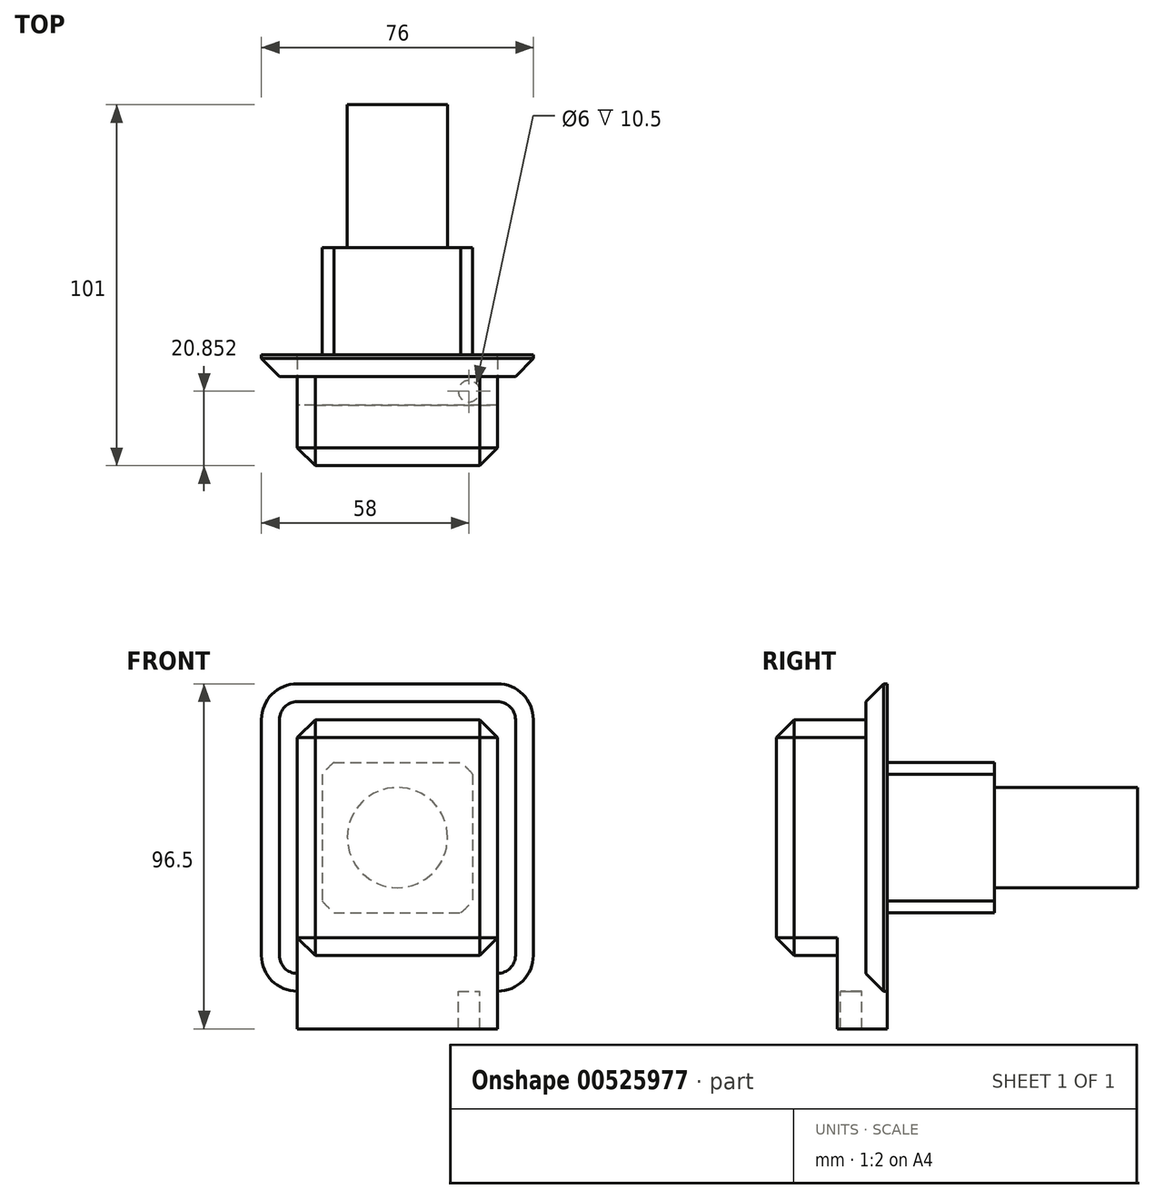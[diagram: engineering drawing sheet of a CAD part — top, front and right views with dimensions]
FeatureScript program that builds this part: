
annotation { "Feature Type Name" : "Feature", "Feature Type Description" : "" }
export const myFeature = defineFeature(function(context is Context, id is Id, definition is map)
    precondition{}
    {
        {
            var Q0;
            Q0=qCreatedBy(makeId("Front.planeOp"),FACE);
            var sketch = newSketch(context, id + "F0", { "sketchPlane" : qUnion([Q0])});
            skLineSegment(sketch, "E0.bottom", {"start": v(28, 43) * mm, "end": v(-28, 43) * mm});
            skLineSegment(sketch, "E0.top", {"start": v(28, -43) * mm, "end": v(-28, -43) * mm});
            skLineSegment(sketch, "E0.left", {"start": v(38, 33) * mm, "end": v(38, -33) * mm});
            skLineSegment(sketch, "E0.right", {"start": v(-38, 33) * mm, "end": v(-38, -33) * mm});
            skPoint(sketch, "E0.middle", {"position": v(0, 0) * mm});
            skPoint(sketch, "E1.visualSharp", {"position": v(-38, 43) * mm});
            skArc(sketch, "E1.filletArc", {"start": v(-28, 43) * mm, "mid": v(-35.07, 40.07) * mm, "end": v(-38, 33) * mm});
            skPoint(sketch, "E2.visualSharp", {"position": v(38, 43) * mm});
            skArc(sketch, "E2.filletArc", {"start": v(38, 33) * mm, "mid": v(35.07, 40.07) * mm, "end": v(28, 43) * mm});
            skPoint(sketch, "E3.visualSharp", {"position": v(38, -43) * mm});
            skArc(sketch, "E3.filletArc", {"start": v(28, -43) * mm, "mid": v(35.07, -40.07) * mm, "end": v(38, -33) * mm});
            skPoint(sketch, "E4.visualSharp", {"position": v(-38, -43) * mm});
            skArc(sketch, "E4.filletArc", {"start": v(-38, -33) * mm, "mid": v(-35.07, -40.07) * mm, "end": v(-28, -43) * mm});
            skSolve(sketch);
        }
        {
            var Q0;
            Q0=qSketchRegion(id+"F0",true);
            extrude(context, id + "F1", {"entities" : qUnion([Q0]), "depth" : 6 * mm, "offsetDistance" : 25 * mm});
        }
        {
            var Q0;
            Q0=makeQuery(id+"F1.opExtrude","CAP_FACE",FACE,{"disambiguationData":[OSD([sQuery(id+"F0.wireOp",EDGE,"E0.bottom"),sQuery(id+"F0.wireOp",EDGE,"E0.top"),sQuery(id+"F0.wireOp",EDGE,"E0.left"),sQuery(id+"F0.wireOp",EDGE,"E0.right")])],"isStart":true});
            var sketch = newSketch(context, id + "F2", { "sketchPlane" : qUnion([Q0])});
            skCircle(sketch, "E5", {"center": v(0, 0) * mm, "radius": 27.5 * mm});
            skSolve(sketch);
        }
        {
            var Q0;
            Q0=qSketchRegion(id+"F2",true);
            extrude(context, id + "F3", {"entities" : qUnion([Q0]), "operationType" : NewBodyOperationType.ADD, "depth" : 30 * mm});
        }
        {
            var Q0;
            Q0=makeQuery(id+"F3.opExtrude","CAP_FACE",FACE,{"disambiguationData":[OSD([sQuery(id+"F2.wireOp",EDGE,"E5")])],"isStart":false});
            var sketch = newSketch(context, id + "F4", { "sketchPlane" : qUnion([Q0])});
            skCircle(sketch, "E6", {"center": v(0, 0) * mm, "radius": 14 * mm});
            skSolve(sketch);
        }
        {
            var Q0;
            Q0=makeQuery(id+"F4.imprint","IMPRINT",FACE,{"disambiguationData":[TD([[makeQuery(id+"F4.imprint","IMPRINT",EDGE,{"derivedFrom":sQuery(id+"F4.wireOp",EDGE,"E6")}),1.0]])]});
            extrude(context, id + "F5", {"entities" : qUnion([Q0]), "operationType" : NewBodyOperationType.ADD, "depth" : 40 * mm});
        }
        {
            var Q0;
            Q0=makeQuery(id+"F1.opExtrude","CAP_FACE",FACE,{"disambiguationData":[OSD([sQuery(id+"F0.wireOp",EDGE,"E0.bottom"),sQuery(id+"F0.wireOp",EDGE,"E0.top"),sQuery(id+"F0.wireOp",EDGE,"E0.left"),sQuery(id+"F0.wireOp",EDGE,"E0.right"),sQuery(id+"F0.wireOp",EDGE,"E1.filletArc"),sQuery(id+"F0.wireOp",EDGE,"E2.filletArc"),sQuery(id+"F0.wireOp",EDGE,"E3.filletArc"),sQuery(id+"F0.wireOp",EDGE,"E4.filletArc")])],"isStart":false});
            var sketch = newSketch(context, id + "F6", { "sketchPlane" : qUnion([Q0])});
            skPoint(sketch, "E7.0", {"position": v(-28, -43) * mm});
            skLineSegment(sketch, "E8.bottom", {"start": v(-28, -43) * mm, "end": v(28, -43) * mm});
            skLineSegment(sketch, "E8.top", {"start": v(-28, -33) * mm, "end": v(28, -33) * mm});
            skLineSegment(sketch, "E8.left", {"start": v(-28, -43) * mm, "end": v(-28, -33) * mm});
            skLineSegment(sketch, "E8.right", {"start": v(28, -43) * mm, "end": v(28, -33) * mm});
            skSolve(sketch);
        }
        {
            var Q0;
            Q0=qSketchRegion(id+"F6",true);
            extrude(context, id + "F7", {"entities" : qUnion([Q0]), "operationType" : NewBodyOperationType.ADD, "depth" : 8 * mm});
        }
        {
            var Q0;
            Q0=makeQuery(id+"F7.boolean.opBoolean","MERGE",FACE,{"derivedFrom":[makeQuery(id+"F1.opExtrude","SWEPT_FACE",FACE,{"disambiguationData":[OSD([sQuery(id+"F0.wireOp",EDGE,"E0.top")])]}),makeQuery(id+"F7.opExtrude","SWEPT_FACE",FACE,{"disambiguationData":[OSD([sQuery(id+"F6.wireOp",EDGE,"E8.bottom")])]})]});
            var sketch = newSketch(context, id + "F8", { "sketchPlane" : qUnion([Q0])});
            skCircle(sketch, "E9", {"center": v(-20, 10.15) * mm, "radius": 3 * mm});
            skCircle(sketch, "E10.MirrorC", {"center": v(20, 10.15) * mm, "radius": 3 * mm});
            skSolve(sketch);
        }
        {
            var Q0;
            Q0=makeQuery(id+"F8.imprint","IMPRINT",FACE,{"disambiguationData":[TD([[makeQuery(id+"F8.imprint","IMPRINT",EDGE,{"derivedFrom":sQuery(id+"F8.wireOp",EDGE,"E9")}),1.0]])]});
            var Q1;
            Q1=makeQuery(id+"F8.imprint","IMPRINT",FACE,{"disambiguationData":[TD([[makeQuery(id+"F8.imprint","IMPRINT",EDGE,{"derivedFrom":sQuery(id+"F8.wireOp",EDGE,"E10.MirrorC")}),-1.0]])]});
            extrude(context, id + "F9", {"entities" : qUnion([Q0, Q1]), "operationType" : NewBodyOperationType.ADD, "depth" : 10.5 * mm});
        }
        {
            var Q0;
            Q0=makeQuery(id+"F1.opExtrude","CAP_FACE",FACE,{"disambiguationData":[OSD([sQuery(id+"F0.wireOp",EDGE,"E0.bottom"),sQuery(id+"F0.wireOp",EDGE,"E0.top"),sQuery(id+"F0.wireOp",EDGE,"E0.left"),sQuery(id+"F0.wireOp",EDGE,"E0.right"),sQuery(id+"F0.wireOp",EDGE,"E1.filletArc"),sQuery(id+"F0.wireOp",EDGE,"E2.filletArc"),sQuery(id+"F0.wireOp",EDGE,"E3.filletArc"),sQuery(id+"F0.wireOp",EDGE,"E4.filletArc")])],"isStart":false});
            var sketch = newSketch(context, id + "F10", { "sketchPlane" : qUnion([Q0])});
            skLineSegment(sketch, "E11.bottom", {"start": v(-28, 33) * mm, "end": v(28, 33) * mm});
            skLineSegment(sketch, "E11.top", {"start": v(-28, -33) * mm, "end": v(28, -33) * mm});
            skLineSegment(sketch, "E11.left", {"start": v(-28, 33) * mm, "end": v(-28, -33) * mm});
            skLineSegment(sketch, "E11.right", {"start": v(28, 33) * mm, "end": v(28, -33) * mm});
            skSolve(sketch);
        }
        {
            var Q0;
            Q0=qSketchRegion(id+"F10",true);
            extrude(context, id + "F11", {"entities" : qUnion([Q0]), "operationType" : NewBodyOperationType.ADD, "depth" : 25 * mm});
        }
        {
            var Q0;
            Q0=makeQuery(id+"F11.opExtrude","CAP_EDGE",EDGE,{"disambiguationData":[OSD([sQuery(id+"F10.wireOp",EDGE,"E11.bottom")])],"isStart":false});
            var Q1;
            Q1=makeQuery(id+"F11.opExtrude","CAP_EDGE",EDGE,{"disambiguationData":[OSD([sQuery(id+"F10.wireOp",EDGE,"E11.right")])],"isStart":false});
            var Q2;
            Q2=makeQuery(id+"F11.opExtrude","CAP_EDGE",EDGE,{"disambiguationData":[OSD([sQuery(id+"F10.wireOp",EDGE,"E11.left")])],"isStart":false});
            var Q3;
            Q3=makeQuery(id+"F11.opExtrude","SWEPT_EDGE",EDGE,{"disambiguationData":[OSD([sQuery(id+"F10.wireOp",EDGE,"E11.bottom"),sQuery(id+"F10.wireOp",EDGE,"E11.left")])]});
            var Q4;
            Q4=makeQuery(id+"F11.opExtrude","SWEPT_EDGE",EDGE,{"disambiguationData":[OSD([sQuery(id+"F10.wireOp",EDGE,"E11.bottom"),sQuery(id+"F10.wireOp",EDGE,"E11.right")])]});
            var Q5;
            Q5=makeQuery(id+"F11.opExtrude","SWEPT_EDGE",EDGE,{"disambiguationData":[OSD([sQuery(id+"F6.wireOp",EDGE,"E8.right"),sQuery(id+"F10.wireOp",EDGE,"E11.top"),sQuery(id+"F10.wireOp",EDGE,"E11.right")])]});
            var Q6;
            Q6=makeQuery(id+"F11.opExtrude","CAP_EDGE",EDGE,{"disambiguationData":[OSD([sQuery(id+"F10.wireOp",EDGE,"E11.top")])],"isStart":false});
            var Q7;
            Q7=makeQuery(id+"F11.opExtrude","SWEPT_EDGE",EDGE,{"disambiguationData":[OSD([sQuery(id+"F6.wireOp",EDGE,"E8.left"),sQuery(id+"F10.wireOp",EDGE,"E11.top"),sQuery(id+"F10.wireOp",EDGE,"E11.left")])]});
            var Q8;
            Q8=makeQuery(id+"F1.opExtrude","CAP_EDGE",EDGE,{"disambiguationData":[OSD([sQuery(id+"F0.wireOp",EDGE,"E0.bottom")])],"isStart":false});
            chamfer(context, id + "F12", {"entities" : qUnion([Q0, Q1, Q2, Q3, Q4, Q5, Q6, Q7, Q8]), "width" : 5 * mm, "tangentPropagation" : true});
        }
        {
            var Q0;
            Q0=makeQuery(id+"F3.opExtrude","CAP_FACE",FACE,{"disambiguationData":[OSD([sQuery(id+"F2.wireOp",EDGE,"E5")])],"isStart":false});
            var sketch = newSketch(context, id + "F13", { "sketchPlane" : qUnion([Q0])});
            skLineSegment(sketch, "E12.bottom", {"start": v(21, 21) * mm, "end": v(-21, 21) * mm});
            skLineSegment(sketch, "E12.top", {"start": v(21, -21) * mm, "end": v(-21, -21) * mm});
            skLineSegment(sketch, "E12.left", {"start": v(21, 21) * mm, "end": v(21, -21) * mm});
            skLineSegment(sketch, "E12.right", {"start": v(-21, 21) * mm, "end": v(-21, -21) * mm});
            skPoint(sketch, "E12.middle", {"position": v(0, 0) * mm});
            skCircle(sketch, "E13.0", {"center": v(0, 0) * mm, "radius": 27.5 * mm});
            skSolve(sketch);
        }
        {
            var Q0;
            {var subQ0=sQuery(id+"F13.wireOp",EDGE,"E13.0");var subQ1=sQuery(id+"F13.wireOp",EDGE,"E12.bottom");var subQ2=makeQuery(id+"F13.imprint","INTERSECT",VERTEX,{"disambiguationData":[OD(0.0)],"derivedFrom":[subQ1,subQ0]});Q0=makeQuery(id+"F13.imprint","IMPRINT",FACE,{"disambiguationData":[TD([[makeQuery(id+"F13.imprint","IMPRINT",EDGE,{"disambiguationData":[TD([[subQ2,-1.0]])],"derivedFrom":subQ1}),-1.0]])]});}
            var Q1;
            {var subQ0=sQuery(id+"F13.wireOp",EDGE,"E13.0");var subQ1=sQuery(id+"F13.wireOp",EDGE,"E12.left");var subQ2=makeQuery(id+"F13.imprint","INTERSECT",VERTEX,{"disambiguationData":[OD(0.0)],"derivedFrom":[subQ1,subQ0]});Q1=makeQuery(id+"F13.imprint","IMPRINT",FACE,{"disambiguationData":[TD([[makeQuery(id+"F13.imprint","IMPRINT",EDGE,{"disambiguationData":[TD([[subQ2,-1.0]])],"derivedFrom":subQ1}),1.0]])]});}
            var Q2;
            {var subQ0=sQuery(id+"F13.wireOp",EDGE,"E13.0");var subQ1=sQuery(id+"F13.wireOp",EDGE,"E12.top");var subQ2=makeQuery(id+"F13.imprint","INTERSECT",VERTEX,{"disambiguationData":[OD(0.0)],"derivedFrom":[subQ1,subQ0]});Q2=makeQuery(id+"F13.imprint","IMPRINT",FACE,{"disambiguationData":[TD([[makeQuery(id+"F13.imprint","IMPRINT",EDGE,{"disambiguationData":[TD([[subQ2,-1.0]])],"derivedFrom":subQ1}),1.0]])]});}
            var Q3;
            {var subQ0=sQuery(id+"F13.wireOp",EDGE,"E13.0");var subQ1=sQuery(id+"F13.wireOp",EDGE,"E12.right");var subQ2=makeQuery(id+"F13.imprint","INTERSECT",VERTEX,{"disambiguationData":[OD(0.0)],"derivedFrom":[subQ1,subQ0]});Q3=makeQuery(id+"F13.imprint","IMPRINT",FACE,{"disambiguationData":[TD([[makeQuery(id+"F13.imprint","IMPRINT",EDGE,{"disambiguationData":[TD([[subQ2,-1.0]])],"derivedFrom":subQ1}),-1.0]])]});}
            var Q4;
            Q4=makeQuery(id+"F1.opExtrude","CAP_FACE",FACE,{"disambiguationData":[OSD([sQuery(id+"F0.wireOp",EDGE,"E0.bottom"),sQuery(id+"F0.wireOp",EDGE,"E0.top"),sQuery(id+"F0.wireOp",EDGE,"E0.left"),sQuery(id+"F0.wireOp",EDGE,"E0.right"),sQuery(id+"F0.wireOp",EDGE,"E1.filletArc"),sQuery(id+"F0.wireOp",EDGE,"E2.filletArc"),sQuery(id+"F0.wireOp",EDGE,"E3.filletArc"),sQuery(id+"F0.wireOp",EDGE,"E4.filletArc")])],"isStart":true});
            extrude(context, id + "F14", {"entities" : qUnion([Q0, Q1, Q2, Q3]), "operationType" : NewBodyOperationType.REMOVE, "endBound" : BoundingType.UP_TO_SURFACE, "oppositeDirection" : true, "depth" : 25 * mm, "endBoundEntityFace" : qUnion([Q4]), "offsetDistance" : 25 * mm});
        }
    });
